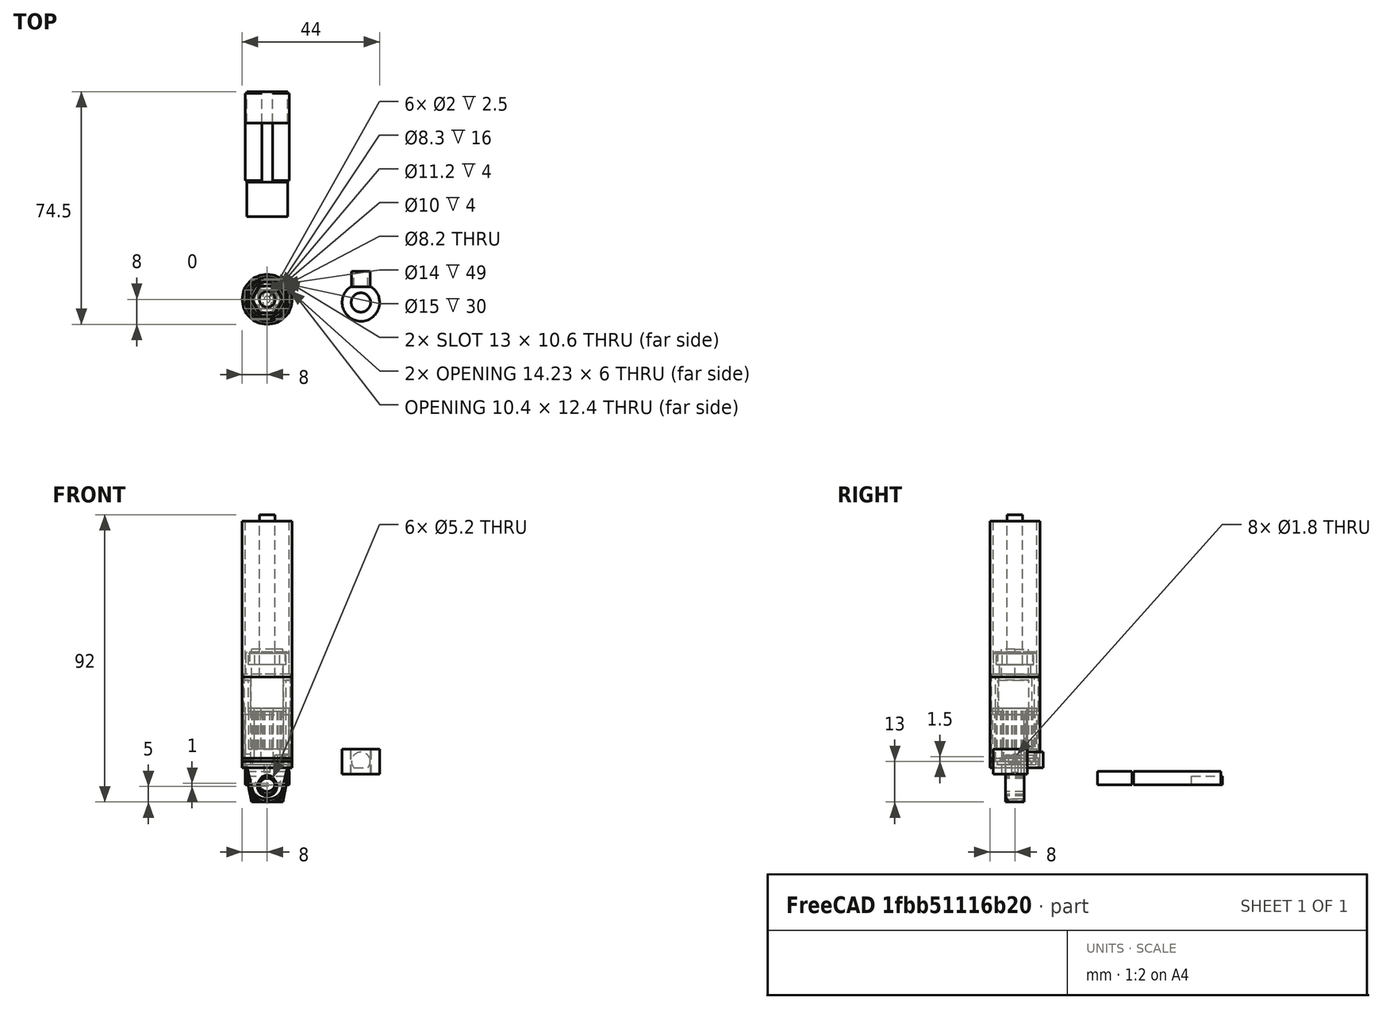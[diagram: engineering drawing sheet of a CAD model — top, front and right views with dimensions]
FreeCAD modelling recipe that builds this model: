
FCSTD DOCUMENT  (FreeCAD 0.18.4R)
Label: crane-cylinder
License: CC-BY 3.0
LicenseURL: http://creativecommons.org/licenses/by/3.0/
objects: Part::Cylinder×114, Part::Cut×95, Part::Box×52, Part::MultiFuse×50, Part::Fillet×11, Part::Cone×10, Part::Chamfer×9, Part::Extrusion×2, App::DocumentObjectGroup×1, Part::RegularPolygon×1, Part::Feature×1
note: 345 computed .brp shape members not serialized (recipe doc carries the construction recipe); baked Part::Feature solids carry a one-line shape summary decoded from their .brp

FEATURE [Part::Cylinder] Cylinder007
  Angle = 360
  AttacherType = Attacher::AttachEngine3D
  Height = 26
  Radius = 7.5
FEATURE [Part::Box] Box  label="Cube"
  AttacherType = Attacher::AttachEngine3D
  Height = 26
  Length = 10.4
  Placement = pos=(-5.2,-8.05,0) rot=(0,0,1;0rad)
  Width = 16.1
FEATURE [Part::Cut] Cut005
  Base = -> Cylinder007
  Refine = true
  Tool = -> Box
FEATURE [Part::Cone] Cone
  Angle = 360
  AttacherType = Attacher::AttachEngine3D
  Height = 13
  Placement = pos=(0,0,-13) rot=(0,0,1;0rad)
  Radius1 = 5
  Radius2 = 7.5
FEATURE [Part::Box] Box001  label="Cube001"
  AttacherType = Attacher::AttachEngine3D
  Height = 12
  Length = 16
  Placement = pos=(-8,3,-12) rot=(0,0,1;0rad)
  Width = 10
FEATURE [Part::Box] Box002  label="Cube002"
  AttacherType = Attacher::AttachEngine3D
  Height = 12
  Length = 16
  Placement = pos=(-8,-13,-12) rot=(0,0,1;0rad)
  Width = 10
FEATURE [Part::MultiFuse] Fusion001
  Placement = pos=(0,0,-1) rot=(0,0,1;0rad)
  Refine = true
  Shapes = -> [Box002,Box001]
FEATURE [Part::Cylinder] Cylinder008
  Angle = 360
  AttacherType = Attacher::AttachEngine3D
  Height = 10
  Placement = pos=(0,5,-8) rot=(1,0,0;1.5708rad)
  Radius = 3.1
FEATURE [Part::Cylinder] Cylinder009
  Angle = 360
  AttacherType = Attacher::AttachEngine3D
  Height = 2
  Placement = pos=(0,0,-2) rot=(0,0,1;0rad)
  Radius = 7.5
FEATURE [Part::Cut] Cut006
  Base = -> Cone
  Refine = true
  Tool = -> Fusion001
FEATURE [Part::MultiFuse] Fusion002
  Refine = true
  Shapes = -> [Cut005,Cut006,Cylinder009]
FEATURE [Part::Cut] Cut007
  Base = -> Fusion002
  Refine = true
  Tool = -> Cylinder008
FEATURE [Part::Box] Box003  label="Cube005"
  AttacherType = Attacher::AttachEngine3D
  Height = 28
  Length = 14
  Placement = pos=(-7,1.5,-2) rot=(0,0,1;0rad)
  Width = 6
FEATURE [Part::Cylinder] Cylinder010
  Angle = 360
  AttacherType = Attacher::AttachEngine3D
  Height = 28
  Placement = pos=(0,0,-2) rot=(0,0,1;0rad)
  Radius = 7.7
FEATURE [Part::Cylinder] Cylinder012
  Angle = 360
  AttacherType = Attacher::AttachEngine3D
  Height = 16
  Radius = 7.5
FEATURE [Part::Cylinder] Cylinder013
  Angle = 360
  AttacherType = Attacher::AttachEngine3D
  Height = 16
  Radius = 6.25
FEATURE [Part::Cut] Cut008
  Base = -> Cylinder012
  Refine = true
  Tool = -> Cylinder013
FEATURE [Part::MultiFuse] Fusion003
  Refine = true
  Shapes = -> [Cut007,Cut008]
FEATURE [Part::Box] Box004  label="Cube006"
  AttacherType = Attacher::AttachEngine3D
  Height = 2.5
  Length = 10
  Placement = pos=(2,-2,-0.5) rot=(0,0,1;0rad)
  Width = 4
FEATURE [Part::Cut] Cut009
  Base = -> Fusion003
  Placement = pos=(0,40,0) rot=(-1,0,0;1.5708rad)
  Refine = true
  Tool = -> Box004
FEATURE [Part::Cut] Cut010  label="cylinder-motor-holder-SUPPORT_"
  Base = -> Box003
  Placement = pos=(0,40,0) rot=(-1,0,0;1.5708rad)
  Refine = true
  Tool = -> Cylinder010
FEATURE [Part::Cylinder] Cylinder014
  Angle = 360
  AttacherType = Attacher::AttachEngine3D
  Height = 5
  Placement = pos=(0,0,4) rot=(0,0,1;0rad)
  Radius = 3
FEATURE [Part::Cylinder] Cylinder015
  Angle = 360
  AttacherType = Attacher::AttachEngine3D
  Height = 8
  Placement = pos=(0,4,0) rot=(1,0,0;1.5708rad)
  Radius = 6
FEATURE [Part::Cylinder] Cylinder016
  Angle = 360
  AttacherType = Attacher::AttachEngine3D
  Height = 8
  Placement = pos=(0,4,0) rot=(1,0,0;1.5708rad)
  Radius = 3.1
FEATURE [Part::Cut] Cut011
  Base = -> Cylinder015
  Placement = pos=(0,0,-1) rot=(0,0,1;0rad)
  Refine = true
  Tool = -> Cylinder016
FEATURE [Part::Box] Box005  label="Cube007"
  AttacherType = Attacher::AttachEngine3D
  Height = 10
  Length = 6
  Placement = pos=(-3,2,4) rot=(0,0,1;0rad)
  Width = 2
FEATURE [Part::Box] Box006  label="Cube009"
  AttacherType = Attacher::AttachEngine3D
  Height = 10
  Length = 10
  Placement = pos=(-5,-5,4) rot=(0,0,1;0rad)
  Width = 10
FEATURE [Part::Cut] Cut012
  Base = -> Cut011
  Refine = true
  Tool = -> Box006
FEATURE [Part::Cut] Cut013
  Base = -> Cylinder014
  Refine = true
  Tool = -> Box005
FEATURE [Part::MultiFuse] Fusion004  label="cylinder-piston-head-attach"
  Placement = pos=(30,0,0) rot=(-1,0,0;1.5708rad)
  Refine = true
  Shapes = -> [Cut012,Cut013]
FEATURE [Part::Fillet] Fillet002  label="cylinder-motor-holder_"
  Base = -> Cut009
  Edges = 3 edges r=3: [Edge56,Edge61,Edge65]
FEATURE [Part::Box] Box008  label="Cube010"
  AttacherType = Attacher::AttachEngine3D
  Height = 3
  Length = 16
  Placement = pos=(-8,56,-7.5) rot=(0,0,1;0rad)
  Width = 10
FEATURE [Part::Cut] Cut  label="cylinder-motor-holder-OLD"
  Base = -> Fillet002
  Placement = pos=(0,0,-40) rot=(1,0,0;1.5708rad)
  Refine = true
  Tool = -> Box008
FEATURE [Part::Box] Box009  label="Cube011"
  AttacherType = Attacher::AttachEngine3D
  Height = 4.3
  Length = 13
  Placement = pos=(-6.5,26.5,-7.5) rot=(0,0,1;0rad)
  Width = 11
FEATURE [Part::Box] Box010  label="Cube012"
  AttacherType = Attacher::AttachEngine3D
  Height = 2.8
  Length = 13
  Placement = pos=(-6.5,56.5,-7.5) rot=(0,0,1;0rad)
  Width = 10
FEATURE [Part::MultiFuse] Fusion  label="cylinder-motor-holder-SUPPORT"
  Refine = true
  Shapes = -> [Box009,Box010]
FEATURE [Part::Cylinder] Cylinder
  Angle = 360
  AttacherType = Attacher::AttachEngine3D
  Height = 4
  Radius = 7.05
FEATURE [Part::Cylinder] Cylinder001
  Angle = 360
  AttacherType = Attacher::AttachEngine3D
  Height = 4
  Radius = 4.1
FEATURE [Part::Cut] Cut014
  Base = -> Cylinder
  Refine = true
  Tool = -> Cylinder001
FEATURE [Part::Cylinder] Cylinder002
  Angle = 360
  AttacherType = Attacher::AttachEngine3D
  Height = 1
  Placement = pos=(0,0,6) rot=(0,0,1;0rad)
  Radius = 8
FEATURE [Part::Cylinder] Cylinder003
  Angle = 360
  AttacherType = Attacher::AttachEngine3D
  Height = 1
  Placement = pos=(0,0,6) rot=(0,0,1;0rad)
  Radius = 6
FEATURE [Part::Cut] Cut001
  Base = -> Cylinder002
  Placement = pos=(0,0,-6) rot=(0,0,1;0rad)
  Refine = true
  Tool = -> Cylinder003
FEATURE [Part::MultiFuse] Fusion005  label="Union"
  Refine = true
  Shapes = -> [Cut001,Cut014]
FEATURE [Part::Chamfer] Chamfer  label="cylinder-jacket-cap"
  Base = -> Fusion005
  Edges = 1 edges r=1: [Edge9]
FEATURE [Part::Cylinder] Cylinder019
  Angle = 360
  AttacherType = Attacher::AttachEngine3D
  Height = 27
  Radius = 8
FEATURE [Part::Box] Box011  label="Cube013"
  AttacherType = Attacher::AttachEngine3D
  Height = 27
  Length = 10.4
  Placement = pos=(-5.2,-6.2,0) rot=(0,0,1;0rad)
  Width = 12.4
FEATURE [Part::Cone] Cone001
  Angle = 360
  AttacherType = Attacher::AttachEngine3D
  Height = 13
  Placement = pos=(0,0,-13) rot=(0,0,1;0rad)
  Radius1 = 5
  Radius2 = 7.5
FEATURE [Part::Box] Box012  label="Cube014"
  AttacherType = Attacher::AttachEngine3D
  Height = 12
  Length = 16
  Placement = pos=(-8,3,-12) rot=(0,0,1;0rad)
  Width = 10
FEATURE [Part::Box] Box013  label="Cube015"
  AttacherType = Attacher::AttachEngine3D
  Height = 12
  Length = 16
  Placement = pos=(-8,-13,-12) rot=(0,0,1;0rad)
  Width = 10
FEATURE [Part::MultiFuse] Fusion006
  Placement = pos=(0,0,-1) rot=(0,0,1;0rad)
  Refine = true
  Shapes = -> [Box013,Box012]
FEATURE [Part::Cut] Cut016
  Base = -> Cone001
  Refine = true
  Tool = -> Fusion006
FEATURE [Part::Cylinder] Cylinder022
  Angle = 360
  AttacherType = Attacher::AttachEngine3D
  Height = 17
  Radius = 8
FEATURE [Part::Cylinder] Cylinder023
  Angle = 360
  AttacherType = Attacher::AttachEngine3D
  Height = 17
  Radius = 6.5
FEATURE [Part::Cut] Cut020
  Base = -> Cylinder022
  Refine = true
  Tool = -> Cylinder023
FEATURE [Part::Fillet] Fillet
  Base = -> Box011
  Edges = 4 edges r=1: [Edge1,Edge3,Edge5,Edge7]
FEATURE [Part::Cut] Cut021
  Base = -> Cylinder019
  Refine = true
  Tool = -> Fillet
FEATURE [Part::MultiFuse] Fusion009
  Refine = true
  Shapes = -> [Cut020,Cut021]
FEATURE [Part::Cylinder] Cylinder028
  Angle = 360
  AttacherType = Attacher::AttachEngine3D
  Height = 27
  Radius = 8
FEATURE [Part::Box] Box017  label="Cube019"
  AttacherType = Attacher::AttachEngine3D
  Height = 27
  Length = 10.4
  Placement = pos=(-5.2,-6.2,0) rot=(0,0,1;0rad)
  Width = 12.4
FEATURE [Part::Cylinder] Cylinder029
  Angle = 360
  AttacherType = Attacher::AttachEngine3D
  Height = 17
  Radius = 8
FEATURE [Part::Cylinder] Cylinder030
  Angle = 360
  AttacherType = Attacher::AttachEngine3D
  Height = 17
  Radius = 6.5
FEATURE [Part::Cut] Cut025
  Base = -> Cylinder029
  Refine = true
  Tool = -> Cylinder030
FEATURE [Part::Fillet] Fillet004
  Base = -> Box017
  Edges = 4 edges r=1: [Edge1,Edge3,Edge5,Edge7]
FEATURE [Part::Cut] Cut026
  Base = -> Cylinder028
  Refine = true
  Tool = -> Fillet004
FEATURE [Part::MultiFuse] Fusion010
  Refine = true
  Shapes = -> [Cut025,Cut026]
FEATURE [Part::Cylinder] Cylinder024
  Angle = 360
  AttacherType = Attacher::AttachEngine3D
  Height = 27
  Radius = 8
FEATURE [Part::Cut] Cut027  label="MOTOR"
  Base = -> Cylinder024
  Refine = true
  Tool = -> Fusion010
FEATURE [Part::Cylinder] Cylinder031
  Angle = 360
  AttacherType = Attacher::AttachEngine3D
  Height = 4
  Radius = 5.6
FEATURE [Part::Cylinder] Cylinder032
  Angle = 360
  AttacherType = Attacher::AttachEngine3D
  Height = 20
  Radius = 6.95
FEATURE [Part::Cylinder] Cylinder033
  Angle = 360
  AttacherType = Attacher::AttachEngine3D
  Height = 8
  Radius = 5
FEATURE [Part::MultiFuse] Fusion011
  Refine = true
  Shapes = -> [Cylinder031,Cylinder033]
FEATURE [Part::Cut] Cut028
  Base = -> Cylinder032
  Refine = true
  Tool = -> Fusion011
FEATURE [Part::Box] Box018  label="Cube020"
  AttacherType = Attacher::AttachEngine3D
  Height = 26
  Length = 10.4
  Placement = pos=(-5.2,-8.05,8) rot=(0,0,1;0rad)
  Width = 16.1
FEATURE [Part::Cylinder] Cylinder034
  Angle = 360
  AttacherType = Attacher::AttachEngine3D
  Height = 16
  Radius = 7.5
FEATURE [Part::Box] Box019  label="Cube021"
  AttacherType = Attacher::AttachEngine3D
  Height = 26
  Length = 10.6
  Placement = pos=(-5.3,-8.05,-1) rot=(0,0,1;0rad)
  Width = 16.1
FEATURE [Part::Cut] Cut030
  Base = -> Cylinder034
  Placement = pos=(0,0,-1) rot=(0,0,1;0rad)
  Refine = true
  Tool = -> Box019
FEATURE [Part::Cone] Cone002
  Angle = 360
  AttacherType = Attacher::AttachEngine3D
  Height = 13
  Placement = pos=(0,0,-13) rot=(0,0,1;0rad)
  Radius1 = 5
  Radius2 = 7.5
FEATURE [Part::Box] Box020  label="Cube022"
  AttacherType = Attacher::AttachEngine3D
  Height = 12
  Length = 16
  Placement = pos=(-8,3,-12) rot=(0,0,1;0rad)
  Width = 10
FEATURE [Part::Box] Box021  label="Cube023"
  AttacherType = Attacher::AttachEngine3D
  Height = 12
  Length = 16
  Placement = pos=(-8,-13,-12) rot=(0,0,1;0rad)
  Width = 10
FEATURE [Part::MultiFuse] Fusion012
  Placement = pos=(0,0,-1) rot=(0,0,1;0rad)
  Refine = true
  Shapes = -> [Box021,Box020]
FEATURE [Part::Cylinder] Cylinder035
  Angle = 360
  AttacherType = Attacher::AttachEngine3D
  Height = 10
  Placement = pos=(0,5,-8) rot=(1,0,0;1.5708rad)
  Radius = 2.6
FEATURE [Part::Cylinder] Cylinder036
  Angle = 360
  AttacherType = Attacher::AttachEngine3D
  Height = 2
  Placement = pos=(0,0,-2) rot=(0,0,1;0rad)
  Radius = 7.5
FEATURE [Part::Cut] Cut031
  Base = -> Cone002
  Refine = true
  Tool = -> Fusion012
FEATURE [Part::Cylinder] Cylinder037
  Angle = 360
  AttacherType = Attacher::AttachEngine3D
  Height = 15
  Radius = 7.5
FEATURE [Part::Cylinder] Cylinder038
  Angle = 360
  AttacherType = Attacher::AttachEngine3D
  Height = 19
  Radius = 6.5
FEATURE [Part::Cut] Cut033
  Base = -> Cylinder037
  Refine = true
  Tool = -> Cylinder038
FEATURE [Part::MultiFuse] Fusion013
  Refine = true
  Shapes = -> [Cut031,Cylinder036]
FEATURE [Part::Cut] Cut034
  Base = -> Fusion013
  Refine = true
  Tool = -> Cylinder035
FEATURE [Part::Cylinder] Cylinder039
  Angle = 360
  AttacherType = Attacher::AttachEngine3D
  Height = 1
  Placement = pos=(0,0,-1) rot=(0,0,1;0rad)
  Radius = 5.5
FEATURE [Part::Cut] Cut035
  Base = -> Cut034
  Refine = true
  Tool = -> Cylinder039
FEATURE [Part::Box] Box022  label="Cube024"
  AttacherType = Attacher::AttachEngine3D
  Height = 3
  Length = 10
  Placement = pos=(2,-3,-1) rot=(0,0,1;0rad)
  Width = 6
FEATURE [Part::Cylinder] Cylinder042
  Angle = 360
  AttacherType = Attacher::AttachEngine3D
  Height = 13
  Placement = pos=(0,0,7) rot=(0,0,1;0rad)
  Radius = 7.45
FEATURE [Part::MultiFuse] Fusion016
  Refine = true
  Shapes = -> [Cut028,Cylinder042]
FEATURE [Part::Fillet] Fillet005
  Base = -> Cut035
  Edges = 3 edges r=4: [Edge1,Edge3,Edge5]
FEATURE [Part::MultiFuse] Fusion017
  Refine = true
  Shapes = -> [Fillet005,Cut030,Cut033]
FEATURE [Part::Cut] Cut039
  Base = -> Fusion017
  Refine = true
  Tool = -> Box022
FEATURE [Part::Cut] Cut041
  Base = -> Fusion016
  Refine = true
  Tool = -> Box018
FEATURE [Part::Cylinder] Cylinder045
  Angle = 360
  AttacherType = Attacher::AttachEngine3D
  Height = 8
  Radius = 5
FEATURE [Part::Cut] Cut042
  Base = -> Cut041
  Placement = pos=(0,0,35) rot=(1,0,0;3.14159rad)
  Refine = true
  Tool = -> Cylinder045
FEATURE [Part::Chamfer] Chamfer001  label="cylinder-motor-holder-bearing-support"
  Base = -> Cut042
  Edges = 1 edges r=0.5: [Edge19]
FEATURE [Part::Cylinder] Cylinder046
  Angle = 360
  AttacherType = Attacher::AttachEngine3D
  Height = 16
  Radius = 7.5
FEATURE [Part::Box] Box023  label="Cube025"
  AttacherType = Attacher::AttachEngine3D
  Height = 26
  Length = 10.6
  Placement = pos=(-5.3,-8.05,-1) rot=(0,0,1;0rad)
  Width = 16.1
FEATURE [Part::Cut] Cut043
  Base = -> Cylinder046
  Placement = pos=(0,0,-1) rot=(0,0,1;0rad)
  Refine = true
  Tool = -> Box023
FEATURE [Part::Cone] Cone003
  Angle = 360
  AttacherType = Attacher::AttachEngine3D
  Height = 13
  Placement = pos=(0,0,-13) rot=(0,0,1;0rad)
  Radius1 = 5
  Radius2 = 7.5
FEATURE [Part::Box] Box024  label="Cube026"
  AttacherType = Attacher::AttachEngine3D
  Height = 12
  Length = 16
  Placement = pos=(-8,3,-12) rot=(0,0,1;0rad)
  Width = 10
FEATURE [Part::Box] Box025  label="Cube027"
  AttacherType = Attacher::AttachEngine3D
  Height = 12
  Length = 16
  Placement = pos=(-8,-13,-12) rot=(0,0,1;0rad)
  Width = 10
FEATURE [Part::MultiFuse] Fusion018
  Placement = pos=(0,0,-1) rot=(0,0,1;0rad)
  Refine = true
  Shapes = -> [Box025,Box024]
FEATURE [Part::Cylinder] Cylinder047
  Angle = 360
  AttacherType = Attacher::AttachEngine3D
  Height = 10
  Placement = pos=(0,5,-8) rot=(1,0,0;1.5708rad)
  Radius = 2.6
FEATURE [Part::Cylinder] Cylinder048
  Angle = 360
  AttacherType = Attacher::AttachEngine3D
  Height = 2
  Placement = pos=(0,0,-2) rot=(0,0,1;0rad)
  Radius = 7.5
FEATURE [Part::Cut] Cut044
  Base = -> Cone003
  Refine = true
  Tool = -> Fusion018
FEATURE [Part::Cylinder] Cylinder049
  Angle = 360
  AttacherType = Attacher::AttachEngine3D
  Height = 15
  Radius = 7.5
FEATURE [Part::Cylinder] Cylinder050
  Angle = 360
  AttacherType = Attacher::AttachEngine3D
  Height = 19
  Radius = 6.5
FEATURE [Part::Cut] Cut045
  Base = -> Cylinder049
  Refine = true
  Tool = -> Cylinder050
FEATURE [Part::MultiFuse] Fusion019
  Refine = true
  Shapes = -> [Cut044,Cylinder048]
FEATURE [Part::Cut] Cut046
  Base = -> Fusion019
  Refine = true
  Tool = -> Cylinder047
FEATURE [Part::Cylinder] Cylinder051
  Angle = 360
  AttacherType = Attacher::AttachEngine3D
  Height = 1
  Placement = pos=(0,0,-1) rot=(0,0,1;0rad)
  Radius = 5.5
FEATURE [Part::Cut] Cut047
  Base = -> Cut046
  Refine = true
  Tool = -> Cylinder051
FEATURE [Part::Box] Box026  label="Cube028"
  AttacherType = Attacher::AttachEngine3D
  Height = 3
  Length = 10
  Placement = pos=(3.46045,-1.01256,-1) rot=(0,0,1;0.698132rad)
  Width = 6
FEATURE [Part::Fillet] Fillet006
  Base = -> Cut047
  Edges = 3 edges r=4: [Edge1,Edge3,Edge5]
FEATURE [Part::MultiFuse] Fusion020
  Refine = true
  Shapes = -> [Fillet006,Cut043,Cut045]
FEATURE [Part::Cut] Cut048
  Base = -> Fusion020
  Refine = true
  Tool = -> Box026
FEATURE [Part::Cylinder] Cylinder052
  Angle = 360
  AttacherType = Attacher::AttachEngine3D
  Height = 16
  Radius = 7.5
FEATURE [Part::Box] Box027  label="Cube029"
  AttacherType = Attacher::AttachEngine3D
  Height = 26
  Length = 10.6
  Placement = pos=(-5.3,-8.05,-1) rot=(0,0,1;0rad)
  Width = 16.1
FEATURE [Part::Cut] Cut049
  Base = -> Cylinder052
  Placement = pos=(0,0,-1) rot=(0,0,1;0rad)
  Refine = true
  Tool = -> Box027
FEATURE [Part::Cone] Cone004
  Angle = 360
  AttacherType = Attacher::AttachEngine3D
  Height = 12
  Placement = pos=(0,0,-12) rot=(0,0,1;0rad)
  Radius1 = 5
  Radius2 = 7.5
FEATURE [Part::Box] Box028  label="Cube030"
  AttacherType = Attacher::AttachEngine3D
  Height = 12
  Length = 16
  Placement = pos=(-8,3,-12) rot=(0,0,1;0rad)
  Width = 10
FEATURE [Part::Box] Box029  label="Cube031"
  AttacherType = Attacher::AttachEngine3D
  Height = 12
  Length = 16
  Placement = pos=(-8,-13,-12) rot=(0,0,1;0rad)
  Width = 10
FEATURE [Part::MultiFuse] Fusion021
  Placement = pos=(0,0,-1) rot=(0,0,1;0rad)
  Refine = true
  Shapes = -> [Box029,Box028]
FEATURE [Part::Cylinder] Cylinder053
  Angle = 360
  AttacherType = Attacher::AttachEngine3D
  Height = 10
  Placement = pos=(0,5,-7) rot=(1,0,0;1.5708rad)
  Radius = 2.6
FEATURE [Part::Cylinder] Cylinder054
  Angle = 360
  AttacherType = Attacher::AttachEngine3D
  Height = 2
  Placement = pos=(0,0,-2) rot=(0,0,1;0rad)
  Radius = 7.5
FEATURE [Part::Cut] Cut050
  Base = -> Cone004
  Refine = true
  Tool = -> Fusion021
FEATURE [Part::Cylinder] Cylinder055
  Angle = 360
  AttacherType = Attacher::AttachEngine3D
  Height = 15
  Radius = 7.5
FEATURE [Part::Cylinder] Cylinder056
  Angle = 360
  AttacherType = Attacher::AttachEngine3D
  Height = 19
  Radius = 6.5
FEATURE [Part::Cut] Cut051
  Base = -> Cylinder055
  Refine = true
  Tool = -> Cylinder056
FEATURE [Part::MultiFuse] Fusion022
  Refine = true
  Shapes = -> [Cut050,Cylinder054]
FEATURE [Part::Cut] Cut052
  Base = -> Fusion022
  Refine = true
  Tool = -> Cylinder053
FEATURE [Part::Cylinder] Cylinder057
  Angle = 360
  AttacherType = Attacher::AttachEngine3D
  Height = 1
  Placement = pos=(0,0,-1) rot=(0,0,1;0rad)
  Radius = 5.5
FEATURE [Part::Cut] Cut053
  Base = -> Cut052
  Refine = true
  Tool = -> Cylinder057
FEATURE [Part::Box] Box030  label="Cube032"
  AttacherType = Attacher::AttachEngine3D
  Height = 3
  Length = 10
  Placement = pos=(2,-3,-1) rot=(0,0,1;0rad)
  Width = 6
FEATURE [Part::Fillet] Fillet007
  Base = -> Cut053
  Edges = 3 edges r=4: [Edge1,Edge3,Edge5]
FEATURE [Part::MultiFuse] Fusion023
  Refine = true
  Shapes = -> [Fillet007,Cut049,Cut051]
FEATURE [Part::Cut] Cut054
  Base = -> Fusion023
  Refine = true
  Tool = -> Box030
FEATURE [Part::Cylinder] Cylinder058
  Angle = 360
  AttacherType = Attacher::AttachEngine3D
  Height = 16
  Radius = 7.5
FEATURE [Part::Box] Box031  label="Cube033"
  AttacherType = Attacher::AttachEngine3D
  Height = 26
  Length = 10.6
  Placement = pos=(-5.3,-8.05,-1) rot=(0,0,1;0rad)
  Width = 16.1
FEATURE [Part::Cut] Cut055
  Base = -> Cylinder058
  Placement = pos=(0,0,-1) rot=(0,0,1;0rad)
  Refine = true
  Tool = -> Box031
FEATURE [Part::Cone] Cone005
  Angle = 360
  AttacherType = Attacher::AttachEngine3D
  Height = 12
  Placement = pos=(0,0,-12) rot=(0,0,1;0rad)
  Radius1 = 5
  Radius2 = 7.5
FEATURE [Part::Box] Box032  label="Cube034"
  AttacherType = Attacher::AttachEngine3D
  Height = 12
  Length = 16
  Placement = pos=(-8,3,-12) rot=(0,0,1;0rad)
  Width = 10
FEATURE [Part::Box] Box033  label="Cube035"
  AttacherType = Attacher::AttachEngine3D
  Height = 12
  Length = 16
  Placement = pos=(-8,-13,-12) rot=(0,0,1;0rad)
  Width = 10
FEATURE [Part::MultiFuse] Fusion024
  Placement = pos=(0,0,-1) rot=(0,0,1;0rad)
  Refine = true
  Shapes = -> [Box033,Box032]
FEATURE [Part::Cylinder] Cylinder059
  Angle = 360
  AttacherType = Attacher::AttachEngine3D
  Height = 10
  Placement = pos=(0,5,-7) rot=(1,0,0;1.5708rad)
  Radius = 2.6
FEATURE [Part::Cylinder] Cylinder060
  Angle = 360
  AttacherType = Attacher::AttachEngine3D
  Height = 2
  Placement = pos=(0,0,-2) rot=(0,0,1;0rad)
  Radius = 7.5
FEATURE [Part::Cut] Cut056
  Base = -> Cone005
  Refine = true
  Tool = -> Fusion024
FEATURE [Part::Cylinder] Cylinder061
  Angle = 360
  AttacherType = Attacher::AttachEngine3D
  Height = 15
  Radius = 7.5
FEATURE [Part::Cylinder] Cylinder062
  Angle = 360
  AttacherType = Attacher::AttachEngine3D
  Height = 19
  Radius = 6.5
FEATURE [Part::Cut] Cut057
  Base = -> Cylinder061
  Refine = true
  Tool = -> Cylinder062
FEATURE [Part::MultiFuse] Fusion025
  Refine = true
  Shapes = -> [Cut056,Cylinder060]
FEATURE [Part::Cut] Cut058
  Base = -> Fusion025
  Refine = true
  Tool = -> Cylinder059
FEATURE [Part::Cylinder] Cylinder063
  Angle = 360
  AttacherType = Attacher::AttachEngine3D
  Height = 1
  Placement = pos=(0,0,-1) rot=(0,0,1;0rad)
  Radius = 5.5
FEATURE [Part::Cut] Cut059
  Base = -> Cut058
  Refine = true
  Tool = -> Cylinder063
FEATURE [Part::Box] Box034  label="Cube036"
  AttacherType = Attacher::AttachEngine3D
  Height = 3
  Length = 10
  Placement = pos=(3.46045,-1.01256,-1) rot=(0,0,1;0.698132rad)
  Width = 6
FEATURE [Part::Fillet] Fillet008
  Base = -> Cut059
  Edges = 3 edges r=4: [Edge1,Edge3,Edge5]
FEATURE [Part::MultiFuse] Fusion026
  Refine = true
  Shapes = -> [Fillet008,Cut055,Cut057]
FEATURE [Part::Cut] Cut060  label="cylinder-main-motor-holder_"
  Base = -> Fusion026
  Refine = true
  Tool = -> Box034
FEATURE [Part::Cylinder] Cylinder064
  Angle = 360
  AttacherType = Attacher::AttachEngine3D
  Height = 4
  Radius = 7.05
FEATURE [Part::Cylinder] Cylinder065
  Angle = 360
  AttacherType = Attacher::AttachEngine3D
  Height = 4
  Radius = 4.15
FEATURE [Part::Cut] Cut061
  Base = -> Cylinder064
  Refine = true
  Tool = -> Cylinder065
FEATURE [Part::Cylinder] Cylinder066
  Angle = 360
  AttacherType = Attacher::AttachEngine3D
  Height = 1
  Placement = pos=(0,0,6) rot=(0,0,1;0rad)
  Radius = 8
FEATURE [Part::Cylinder] Cylinder067
  Angle = 360
  AttacherType = Attacher::AttachEngine3D
  Height = 1
  Placement = pos=(0,0,6) rot=(0,0,1;0rad)
  Radius = 6
FEATURE [Part::Cut] Cut062
  Base = -> Cylinder066
  Placement = pos=(0,0,-6) rot=(0,0,1;0rad)
  Refine = true
  Tool = -> Cylinder067
FEATURE [Part::MultiFuse] Fusion027  label="Union001"
  Refine = true
  Shapes = -> [Cut062,Cut061]
FEATURE [Part::Chamfer] Chamfer002  label="cylinder-jacket-cap001"
  Base = -> Fusion027
  Edges = 1 edges r=1: [Edge9]
FEATURE [Part::Cylinder] Cylinder068
  Angle = 45
  AttacherType = Attacher::AttachEngine3D
  Height = 16
  Radius = 7
FEATURE [Part::Cylinder] Cylinder069
  Angle = 360
  AttacherType = Attacher::AttachEngine3D
  Height = 16
  Radius = 4.15
FEATURE [Part::Cut] Cut063
  Base = -> Cylinder068
  Placement = pos=(0,0,1) rot=(0,0,1;0rad)
  Refine = true
  Tool = -> Cylinder069
FEATURE [Part::Cylinder] Cylinder070
  Angle = 360
  AttacherType = Attacher::AttachEngine3D
  Height = 16
  Radius = 7.05
FEATURE [Part::Cylinder] Cylinder071
  Angle = 360
  AttacherType = Attacher::AttachEngine3D
  Height = 16
  Radius = 6
FEATURE [Part::Cut] Cut064
  Base = -> Cylinder070
  Placement = pos=(0,0,1) rot=(0,0,1;0rad)
  Refine = true
  Tool = -> Cylinder071
FEATURE [Part::Chamfer] Chamfer003
  Base = -> Cut063
  Edges = 2 edges r=0.5: [Edge9,Edge12]
FEATURE [Part::Cylinder] Cylinder072
  Angle = 45
  AttacherType = Attacher::AttachEngine3D
  Height = 16
  Radius = 7
FEATURE [Part::Cylinder] Cylinder073
  Angle = 360
  AttacherType = Attacher::AttachEngine3D
  Height = 16
  Radius = 4.15
FEATURE [Part::Cut] Cut065
  Base = -> Cylinder072
  Placement = pos=(0,0,1) rot=(0,0,1;0rad)
  Refine = true
  Tool = -> Cylinder073
FEATURE [Part::Chamfer] Chamfer004
  Base = -> Cut065
  Edges = 2 edges r=0.5: [Edge9,Edge12]
  Placement = pos=(0,0,0) rot=(0,0,1;1.25664rad)
FEATURE [Part::Cylinder] Cylinder074
  Angle = 45
  AttacherType = Attacher::AttachEngine3D
  Height = 16
  Radius = 7
FEATURE [Part::Cylinder] Cylinder075
  Angle = 360
  AttacherType = Attacher::AttachEngine3D
  Height = 16
  Radius = 4.15
FEATURE [Part::Cut] Cut066
  Base = -> Cylinder074
  Placement = pos=(0,0,1) rot=(0,0,1;0rad)
  Refine = true
  Tool = -> Cylinder075
FEATURE [Part::Chamfer] Chamfer005
  Base = -> Cut066
  Edges = 2 edges r=0.5: [Edge9,Edge12]
  Placement = pos=(0,0,0) rot=(0,0,1;2.51327rad)
FEATURE [Part::Cylinder] Cylinder076
  Angle = 45
  AttacherType = Attacher::AttachEngine3D
  Height = 16
  Radius = 7
FEATURE [Part::Cylinder] Cylinder077
  Angle = 360
  AttacherType = Attacher::AttachEngine3D
  Height = 16
  Radius = 4.15
FEATURE [Part::Cut] Cut067
  Base = -> Cylinder076
  Placement = pos=(0,0,1) rot=(0,0,1;0rad)
  Refine = true
  Tool = -> Cylinder077
FEATURE [Part::Chamfer] Chamfer006
  Base = -> Cut067
  Edges = 2 edges r=0.5: [Edge9,Edge12]
  Placement = pos=(0,0,0) rot=(0,0,1;3.76991rad)
FEATURE [Part::Cylinder] Cylinder078
  Angle = 45
  AttacherType = Attacher::AttachEngine3D
  Height = 16
  Radius = 7
FEATURE [Part::Cylinder] Cylinder079
  Angle = 360
  AttacherType = Attacher::AttachEngine3D
  Height = 16
  Radius = 4.15
FEATURE [Part::Cut] Cut068
  Base = -> Cylinder078
  Placement = pos=(0,0,1) rot=(0,0,1;0rad)
  Refine = true
  Tool = -> Cylinder079
FEATURE [Part::Chamfer] Chamfer007
  Base = -> Cut068
  Edges = 2 edges r=0.5: [Edge9,Edge12]
  Placement = pos=(0,0,0) rot=(0,0,-1;1.25664rad)
FEATURE [Part::MultiFuse] Fusion028
  Refine = true
  Shapes = -> [Chamfer004,Chamfer003,Chamfer007,Chamfer005,Chamfer006]
FEATURE [Part::MultiFuse] Fusion029
  Refine = true
  Shapes = -> [Fusion028,Cut064]
FEATURE [Part::MultiFuse] Fusion030  label="cylinder-jacket-cap-001"
  Refine = true
  Shapes = -> [Chamfer002,Fusion029]
FEATURE [Part::Cylinder] Cylinder080
  Angle = 360
  AttacherType = Attacher::AttachEngine3D
  Height = 2
  Placement = pos=(0,0,-2) rot=(0,0,1;0rad)
  Radius = 7.5
FEATURE [Part::Cylinder] Cylinder081
  Angle = 360
  AttacherType = Attacher::AttachEngine3D
  Height = 16
  Radius = 7.5
FEATURE [Part::Box] Box035  label="Cube037"
  AttacherType = Attacher::AttachEngine3D
  Height = 26
  Length = 10.6
  Placement = pos=(-5.3,-8.05,-1) rot=(0,0,1;0rad)
  Width = 16.1
FEATURE [Part::Cut] Cut069
  Base = -> Cylinder081
  Placement = pos=(0,0,-1) rot=(0,0,1;0rad)
  Refine = true
  Tool = -> Box035
FEATURE [Part::Cone] Cone006
  Angle = 360
  AttacherType = Attacher::AttachEngine3D
  Height = 12
  Placement = pos=(0,0,-12) rot=(0,0,1;0rad)
  Radius1 = 5
  Radius2 = 7.5
FEATURE [Part::Box] Box036  label="Cube038"
  AttacherType = Attacher::AttachEngine3D
  Height = 12
  Length = 16
  Placement = pos=(-8,3,-12) rot=(0,0,1;0rad)
  Width = 10
FEATURE [Part::Box] Box037  label="Cube039"
  AttacherType = Attacher::AttachEngine3D
  Height = 12
  Length = 16
  Placement = pos=(-8,-13,-12) rot=(0,0,1;0rad)
  Width = 10
FEATURE [Part::MultiFuse] Fusion031
  Placement = pos=(0,0,-1) rot=(0,0,1;0rad)
  Refine = true
  Shapes = -> [Box037,Box036]
FEATURE [Part::Cylinder] Cylinder082
  Angle = 360
  AttacherType = Attacher::AttachEngine3D
  Height = 10
  Placement = pos=(0,5,-7) rot=(1,0,0;1.5708rad)
  Radius = 2.6
FEATURE [Part::Cut] Cut070
  Base = -> Cone006
  Refine = true
  Tool = -> Fusion031
FEATURE [Part::Cylinder] Cylinder083
  Angle = 360
  AttacherType = Attacher::AttachEngine3D
  Height = 15
  Radius = 7.5
FEATURE [Part::Cylinder] Cylinder084
  Angle = 360
  AttacherType = Attacher::AttachEngine3D
  Height = 19
  Radius = 6.5
FEATURE [Part::Cut] Cut071
  Base = -> Cylinder083
  Refine = true
  Tool = -> Cylinder084
FEATURE [Part::MultiFuse] Fusion032
  Refine = true
  Shapes = -> [Cut070,Cylinder080]
FEATURE [Part::Cut] Cut072
  Base = -> Fusion032
  Refine = true
  Tool = -> Cylinder082
FEATURE [Part::Cylinder] Cylinder085
  Angle = 360
  AttacherType = Attacher::AttachEngine3D
  Height = 1
  Placement = pos=(0,0,-1) rot=(0,0,1;0rad)
  Radius = 5.5
FEATURE [Part::Cut] Cut073
  Base = -> Cut072
  Refine = true
  Tool = -> Cylinder085
FEATURE [Part::Box] Box038  label="Cube040"
  AttacherType = Attacher::AttachEngine3D
  Height = 3
  Length = 10
  Placement = pos=(3.46045,-1.01256,-1) rot=(0,0,1;0.698132rad)
  Width = 6
FEATURE [Part::Fillet] Fillet009
  Base = -> Cut073
  Edges = 3 edges r=4: [Edge1,Edge3,Edge5]
FEATURE [Part::MultiFuse] Fusion033
  Refine = true
  Shapes = -> [Fillet009,Cut069,Cut071]
FEATURE [Part::Cut] Cut074  label="cylinder-motor-holder-short-30-deg-exit001"
  Base = -> Fusion033
  Refine = true
  Tool = -> Box038
FEATURE [Part::Box] Box039  label="Cube041"
  AttacherType = Attacher::AttachEngine3D
  Height = 27
  Length = 16
  Placement = pos=(-8,3,-12) rot=(0,0,1;0rad)
  Width = 10
FEATURE [Part::Box] Box040  label="Cube042"
  AttacherType = Attacher::AttachEngine3D
  Height = 27
  Length = 16
  Placement = pos=(-8,-9,-12) rot=(0,0,1;0rad)
  Width = 12
FEATURE [Part::Cylinder] Cylinder086
  Angle = 360
  AttacherType = Attacher::AttachEngine3D
  Height = 16
  Radius = 7.5
FEATURE [Part::Cylinder] Cylinder087
  Angle = 360
  AttacherType = Attacher::AttachEngine3D
  Height = 10
  Placement = pos=(0,5,-7) rot=(1,0,0;1.5708rad)
  Radius = 2.6
FEATURE [Part::Box] Box041  label="Cube043"
  AttacherType = Attacher::AttachEngine3D
  Height = 12
  Length = 16
  Placement = pos=(-8,-13,-12) rot=(0,0,1;0rad)
  Width = 10
FEATURE [Part::Box] Box042  label="Cube044"
  AttacherType = Attacher::AttachEngine3D
  Height = 12
  Length = 16
  Placement = pos=(-8,3,-12) rot=(0,0,1;0rad)
  Width = 10
FEATURE [Part::MultiFuse] Fusion034
  Placement = pos=(0,0,-1) rot=(0,0,1;0rad)
  Refine = true
  Shapes = -> [Box041,Box042]
FEATURE [Part::Box] Box043  label="Cube045"
  AttacherType = Attacher::AttachEngine3D
  Height = 26
  Length = 10.6
  Placement = pos=(-5.3,-8.05,-1) rot=(0,0,1;0rad)
  Width = 16.1
FEATURE [Part::Cylinder] Cylinder088
  Angle = 360
  AttacherType = Attacher::AttachEngine3D
  Height = 2
  Placement = pos=(0,0,-2) rot=(0,0,1;0rad)
  Radius = 7.5
FEATURE [Part::Cone] Cone007
  Angle = 360
  AttacherType = Attacher::AttachEngine3D
  Height = 12
  Placement = pos=(0,0,-12) rot=(0,0,1;0rad)
  Radius1 = 5
  Radius2 = 7.5
FEATURE [Part::Cut] Cut079
  Base = -> Cone007
  Refine = true
  Tool = -> Fusion034
FEATURE [Part::MultiFuse] Fusion036
  Refine = true
  Shapes = -> [Cut079,Cylinder088]
FEATURE [Part::Cut] Cut077
  Base = -> Fusion036
  Refine = true
  Tool = -> Cylinder087
FEATURE [Part::Cut] Cut080
  Base = -> Cylinder086
  Placement = pos=(0,0,-1) rot=(0,0,1;0rad)
  Refine = true
  Tool = -> Box043
FEATURE [Part::Cylinder] Cylinder089
  Angle = 360
  AttacherType = Attacher::AttachEngine3D
  Height = 19
  Radius = 6.5
FEATURE [Part::Cylinder] Cylinder090
  Angle = 360
  AttacherType = Attacher::AttachEngine3D
  Height = 15
  Radius = 7.5
FEATURE [Part::Cut] Cut078
  Base = -> Cylinder090
  Refine = true
  Tool = -> Cylinder089
FEATURE [Part::Cylinder] Cylinder091
  Angle = 360
  AttacherType = Attacher::AttachEngine3D
  Height = 1
  Placement = pos=(0,0,-1) rot=(0,0,1;0rad)
  Radius = 5.5
FEATURE [Part::Cut] Cut076
  Base = -> Cut077
  Refine = true
  Tool = -> Cylinder091
FEATURE [Part::Fillet] Fillet010
  Base = -> Cut076
  Edges = 3 edges r=4: [Edge1,Edge3,Edge5]
FEATURE [Part::MultiFuse] Fusion035
  Refine = true
  Shapes = -> [Fillet010,Cut080,Cut078]
FEATURE [Part::Box] Box044  label="Cube046"
  AttacherType = Attacher::AttachEngine3D
  Height = 3
  Length = 10
  Placement = pos=(3.46045,-1.01256,-1) rot=(0,0,1;0.698132rad)
  Width = 6
FEATURE [Part::Cut] Cut075  label="cylinder-motor-holder-short-30-deg-exit002"
  Base = -> Fusion035
  Refine = true
  Tool = -> Box044
FEATURE [Part::Cut] Cut081
  Base = -> Cut074
  Refine = true
  Tool = -> Box039
FEATURE [Part::Cut] Cut082  label="cylinder-main-motor-holder_B"
  Base = -> Cut075
  Refine = true
  Tool = -> Box040
FEATURE [Part::Cylinder] Cylinder092
  Angle = 360
  AttacherType = Attacher::AttachEngine3D
  Height = 10
  Placement = pos=(0,0,-3.5) rot=(0,0,1;0rad)
  Radius = 1
FEATURE [Part::Cut] Cut083
  Base = -> Cut081
  Refine = true
  Tool = -> Cylinder092
FEATURE [Part::Cylinder] Cylinder093
  Angle = 360
  AttacherType = Attacher::AttachEngine3D
  Height = 13
  Placement = pos=(-9,0,1.5) rot=(0,1,0;1.5708rad)
  Radius = 0.9
FEATURE [Part::Cut] Cut084  label="cylinder-main-motor-holder_A"
  Base = -> Cut083
  Refine = true
  Tool = -> Cylinder093
FEATURE [Part::Cylinder] Cylinder094
  Angle = 360
  AttacherType = Attacher::AttachEngine3D
  Height = 10
  Placement = pos=(0,0,-3.5) rot=(0,0,1;0rad)
  Radius = 1
FEATURE [Part::Cylinder] Cylinder095
  Angle = 360
  AttacherType = Attacher::AttachEngine3D
  Height = 18
  Placement = pos=(-9,0,1.5) rot=(0,1,0;1.5708rad)
  Radius = 0.9
FEATURE [Part::MultiFuse] Fusion037
  Refine = true
  Shapes = -> [Cylinder094,Cylinder095]
FEATURE [Part::Cut] Cut085  label="cylinder-main-motor-holder"
  Base = -> Cut060
  Refine = true
  Tool = -> Fusion037
FEATURE [Part::Cylinder] Cylinder096
  Angle = 360
  AttacherType = Attacher::AttachEngine3D
  Height = 10
  Placement = pos=(0,0,-3.5) rot=(0,0,1;0rad)
  Radius = 1
FEATURE [Part::Cylinder] Cylinder097
  Angle = 360
  AttacherType = Attacher::AttachEngine3D
  Height = 14
  Placement = pos=(-9,0,1.5) rot=(0,1,0;1.5708rad)
  Radius = 0.9
FEATURE [Part::MultiFuse] Fusion038
  Refine = true
  Shapes = -> [Cylinder096,Cylinder097]
FEATURE [Part::Cut] Cut086  label="cylinder-main-motor-holder-straight-exit"
  Base = -> Cut054
  Refine = true
  Tool = -> Fusion038
FEATURE [Part::Cylinder] Cylinder098
  Angle = 360
  AttacherType = Attacher::AttachEngine3D
  Height = 10
  Placement = pos=(0,0,-3.5) rot=(0,0,1;0rad)
  Radius = 1
FEATURE [Part::Cylinder] Cylinder099
  Angle = 360
  AttacherType = Attacher::AttachEngine3D
  Height = 18
  Placement = pos=(-9,0,1.5) rot=(0,1,0;1.5708rad)
  Radius = 0.9
FEATURE [Part::MultiFuse] Fusion039
  Refine = true
  Shapes = -> [Cylinder098,Cylinder099]
FEATURE [Part::Cut] Cut087  label="cylinder-main-motor-holder-long"
  Base = -> Cut048
  Refine = true
  Tool = -> Fusion039
FEATURE [App::DocumentObjectGroup] Group  label="backup"
  Group = -> [Fusion030,Cut086,Cut087,Cut010,Fusion004,Cut,Fusion,Cut016,Fusion009]
FEATURE [Part::Cylinder] Cylinder100
  Angle = 360
  AttacherType = Attacher::AttachEngine3D
  Height = 10
  Placement = pos=(0,0,-3.5) rot=(0,0,1;0rad)
  Radius = 1
FEATURE [Part::Cylinder] Cylinder101
  Angle = 360
  AttacherType = Attacher::AttachEngine3D
  Height = 14
  Placement = pos=(-9,0,0) rot=(0,1,0;1.5708rad)
  Radius = 0.9
FEATURE [Part::MultiFuse] Fusion040
  Refine = true
  Shapes = -> [Cylinder100,Cylinder101]
FEATURE [Part::Cut] Cut088  label="cylinder-extender-motor-holder"
  Base = -> Cut039
  Refine = true
  Tool = -> Fusion040
FEATURE [Part::Box] Box045  label="Cube047"
  AttacherType = Attacher::AttachEngine3D
  Height = 30
  Length = 16
  Placement = pos=(-8,-9,-14) rot=(0,0,1;0rad)
  Width = 12
FEATURE [Part::Box] Box046  label="Cube048"
  AttacherType = Attacher::AttachEngine3D
  Height = 30
  Length = 16
  Placement = pos=(-8,3,-14) rot=(0,0,1;0rad)
  Width = 10
FEATURE [Part::Cylinder] Cylinder102
  Angle = 360
  AttacherType = Attacher::AttachEngine3D
  Height = 16
  Radius = 7.5
FEATURE [Part::Box] Box047  label="Cube049"
  AttacherType = Attacher::AttachEngine3D
  Height = 26
  Length = 10.6
  Placement = pos=(-5.3,-8.05,-1) rot=(0,0,1;0rad)
  Width = 16.1
FEATURE [Part::Cut] Cut089
  Base = -> Cylinder102
  Placement = pos=(0,0,-1) rot=(0,0,1;0rad)
  Refine = true
  Tool = -> Box047
FEATURE [Part::Cone] Cone008
  Angle = 360
  AttacherType = Attacher::AttachEngine3D
  Height = 13
  Placement = pos=(0,0,-13) rot=(0,0,1;0rad)
  Radius1 = 5
  Radius2 = 7.5
FEATURE [Part::Box] Box048  label="Cube050"
  AttacherType = Attacher::AttachEngine3D
  Height = 12
  Length = 16
  Placement = pos=(-8,3,-12) rot=(0,0,1;0rad)
  Width = 10
FEATURE [Part::Box] Box049  label="Cube051"
  AttacherType = Attacher::AttachEngine3D
  Height = 12
  Length = 16
  Placement = pos=(-8,-13,-12) rot=(0,0,1;0rad)
  Width = 10
FEATURE [Part::MultiFuse] Fusion041
  Placement = pos=(0,0,-1) rot=(0,0,1;0rad)
  Refine = true
  Shapes = -> [Box049,Box048]
FEATURE [Part::Cylinder] Cylinder103
  Angle = 360
  AttacherType = Attacher::AttachEngine3D
  Height = 10
  Placement = pos=(0,5,-8) rot=(1,0,0;1.5708rad)
  Radius = 2.6
FEATURE [Part::Cylinder] Cylinder104
  Angle = 360
  AttacherType = Attacher::AttachEngine3D
  Height = 2
  Placement = pos=(0,0,-2) rot=(0,0,1;0rad)
  Radius = 7.5
FEATURE [Part::Cut] Cut090
  Base = -> Cone008
  Refine = true
  Tool = -> Fusion041
FEATURE [Part::Cylinder] Cylinder105
  Angle = 360
  AttacherType = Attacher::AttachEngine3D
  Height = 15
  Radius = 7.5
FEATURE [Part::Cylinder] Cylinder106
  Angle = 360
  AttacherType = Attacher::AttachEngine3D
  Height = 19
  Radius = 6.5
FEATURE [Part::Cut] Cut091
  Base = -> Cylinder105
  Refine = true
  Tool = -> Cylinder106
FEATURE [Part::MultiFuse] Fusion042
  Refine = true
  Shapes = -> [Cut090,Cylinder104]
FEATURE [Part::Cut] Cut092
  Base = -> Fusion042
  Refine = true
  Tool = -> Cylinder103
FEATURE [Part::Cylinder] Cylinder107
  Angle = 360
  AttacherType = Attacher::AttachEngine3D
  Height = 1
  Placement = pos=(0,0,-1) rot=(0,0,1;0rad)
  Radius = 5.5
FEATURE [Part::Cut] Cut093
  Base = -> Cut092
  Refine = true
  Tool = -> Cylinder107
FEATURE [Part::Fillet] Fillet011
  Base = -> Cut093
  Edges = 3 edges r=4: [Edge1,Edge3,Edge5]
FEATURE [Part::Box] Box050  label="Cube052"
  AttacherType = Attacher::AttachEngine3D
  Height = 3
  Length = 10
  Placement = pos=(2,-3,-1) rot=(0,0,1;0rad)
  Width = 6
FEATURE [Part::MultiFuse] Fusion043
  Refine = true
  Shapes = -> [Fillet011,Cut089,Cut091]
FEATURE [Part::Cut] Cut094
  Base = -> Fusion043
  Refine = true
  Tool = -> Box050
FEATURE [Part::Cylinder] Cylinder108
  Angle = 360
  AttacherType = Attacher::AttachEngine3D
  Height = 10
  Placement = pos=(0,0,-3.5) rot=(0,0,1;0rad)
  Radius = 1
FEATURE [Part::Cylinder] Cylinder109
  Angle = 360
  AttacherType = Attacher::AttachEngine3D
  Height = 14
  Placement = pos=(-9,0,0) rot=(0,1,0;1.5708rad)
  Radius = 0.9
FEATURE [Part::MultiFuse] Fusion044
  Refine = true
  Shapes = -> [Cylinder108,Cylinder109]
FEATURE [Part::Cut] Cut095  label="cylinder-extender-motor-holder001"
  Base = -> Cut094
  Refine = true
  Tool = -> Fusion044
FEATURE [Part::Cylinder] Cylinder110
  Angle = 360
  AttacherType = Attacher::AttachEngine3D
  Height = 16
  Radius = 7.5
FEATURE [Part::Box] Box051  label="Cube053"
  AttacherType = Attacher::AttachEngine3D
  Height = 26
  Length = 10.6
  Placement = pos=(-5.3,-8.05,-1) rot=(0,0,1;0rad)
  Width = 16.1
FEATURE [Part::Cut] Cut096
  Base = -> Cylinder110
  Placement = pos=(0,0,-1) rot=(0,0,1;0rad)
  Refine = true
  Tool = -> Box051
FEATURE [Part::Cone] Cone009
  Angle = 360
  AttacherType = Attacher::AttachEngine3D
  Height = 13
  Placement = pos=(0,0,-13) rot=(0,0,1;0rad)
  Radius1 = 5
  Radius2 = 7.5
FEATURE [Part::Box] Box052  label="Cube054"
  AttacherType = Attacher::AttachEngine3D
  Height = 12
  Length = 16
  Placement = pos=(-8,3,-12) rot=(0,0,1;0rad)
  Width = 10
FEATURE [Part::Box] Box053  label="Cube055"
  AttacherType = Attacher::AttachEngine3D
  Height = 12
  Length = 16
  Placement = pos=(-8,-13,-12) rot=(0,0,1;0rad)
  Width = 10
FEATURE [Part::MultiFuse] Fusion045
  Placement = pos=(0,0,-1) rot=(0,0,1;0rad)
  Refine = true
  Shapes = -> [Box053,Box052]
FEATURE [Part::Cylinder] Cylinder111
  Angle = 360
  AttacherType = Attacher::AttachEngine3D
  Height = 10
  Placement = pos=(0,5,-8) rot=(1,0,0;1.5708rad)
  Radius = 2.6
FEATURE [Part::Cylinder] Cylinder112
  Angle = 360
  AttacherType = Attacher::AttachEngine3D
  Height = 2
  Placement = pos=(0,0,-2) rot=(0,0,1;0rad)
  Radius = 7.5
FEATURE [Part::Cut] Cut097
  Base = -> Cone009
  Refine = true
  Tool = -> Fusion045
FEATURE [Part::Cylinder] Cylinder113
  Angle = 360
  AttacherType = Attacher::AttachEngine3D
  Height = 15
  Radius = 7.5
FEATURE [Part::Cylinder] Cylinder114
  Angle = 360
  AttacherType = Attacher::AttachEngine3D
  Height = 19
  Radius = 6.5
FEATURE [Part::Cut] Cut098
  Base = -> Cylinder113
  Refine = true
  Tool = -> Cylinder114
FEATURE [Part::MultiFuse] Fusion046
  Refine = true
  Shapes = -> [Cut097,Cylinder112]
FEATURE [Part::Cut] Cut099
  Base = -> Fusion046
  Refine = true
  Tool = -> Cylinder111
FEATURE [Part::Cylinder] Cylinder115
  Angle = 360
  AttacherType = Attacher::AttachEngine3D
  Height = 1
  Placement = pos=(0,0,-1) rot=(0,0,1;0rad)
  Radius = 5.5
FEATURE [Part::Cut] Cut100
  Base = -> Cut099
  Refine = true
  Tool = -> Cylinder115
FEATURE [Part::Fillet] Fillet012
  Base = -> Cut100
  Edges = 3 edges r=4: [Edge1,Edge3,Edge5]
FEATURE [Part::Box] Box054  label="Cube056"
  AttacherType = Attacher::AttachEngine3D
  Height = 3
  Length = 10
  Placement = pos=(2,-3,-1) rot=(0,0,1;0rad)
  Width = 6
FEATURE [Part::MultiFuse] Fusion047
  Refine = true
  Shapes = -> [Fillet012,Cut096,Cut098]
FEATURE [Part::Cut] Cut101
  Base = -> Fusion047
  Refine = true
  Tool = -> Box054
FEATURE [Part::Cylinder] Cylinder116
  Angle = 360
  AttacherType = Attacher::AttachEngine3D
  Height = 10
  Placement = pos=(0,0,-3.5) rot=(0,0,1;0rad)
  Radius = 1
FEATURE [Part::Cylinder] Cylinder117
  Angle = 360
  AttacherType = Attacher::AttachEngine3D
  Height = 14
  Placement = pos=(-9,0,0) rot=(0,1,0;1.5708rad)
  Radius = 0.9
FEATURE [Part::MultiFuse] Fusion048
  Refine = true
  Shapes = -> [Cylinder116,Cylinder117]
FEATURE [Part::Cut] Cut102  label="cylinder-extender-motor-holder002"
  Base = -> Cut101
  Refine = true
  Tool = -> Fusion048
FEATURE [Part::Cut] Cut103  label="cylinder-extender-motor-holder_B"
  Base = -> Cut095
  Refine = true
  Tool = -> Box045
FEATURE [Part::Cut] Cut104  label="cylinder-extender-motor-holder_A"
  Base = -> Cut102
  Refine = true
  Tool = -> Box046
FEATURE [Part::Cylinder] Cylinder118
  Angle = 360
  AttacherType = Attacher::AttachEngine3D
  Height = 4
  Radius = 5.7
FEATURE [Part::Cylinder] Cylinder119
  Angle = 360
  AttacherType = Attacher::AttachEngine3D
  Height = 20
  Radius = 6.85
FEATURE [Part::Cylinder] Cylinder120
  Angle = 360
  AttacherType = Attacher::AttachEngine3D
  Height = 8
  Radius = 5
FEATURE [Part::MultiFuse] Fusion049
  Refine = true
  Shapes = -> [Cylinder118,Cylinder120]
FEATURE [Part::Cut] Cut105
  Base = -> Cylinder119
  Refine = true
  Tool = -> Fusion049
FEATURE [Part::Box] Box055  label="Cube057"
  AttacherType = Attacher::AttachEngine3D
  Height = 26
  Length = 10.4
  Placement = pos=(-5.2,-8.05,8) rot=(0,0,1;0rad)
  Width = 16.1
FEATURE [Part::Cylinder] Cylinder121
  Angle = 360
  AttacherType = Attacher::AttachEngine3D
  Height = 13
  Placement = pos=(0,0,7) rot=(0,0,1;0rad)
  Radius = 7.45
FEATURE [Part::MultiFuse] Fusion050
  Refine = true
  Shapes = -> [Cut105,Cylinder121]
FEATURE [Part::Cut] Cut106
  Base = -> Fusion050
  Refine = true
  Tool = -> Box055
FEATURE [Part::Cylinder] Cylinder122
  Angle = 360
  AttacherType = Attacher::AttachEngine3D
  Height = 8
  Radius = 5
FEATURE [Part::Cut] Cut107
  Base = -> Cut106
  Placement = pos=(0,0,35) rot=(1,0,0;3.14159rad)
  Refine = true
  Tool = -> Cylinder122
FEATURE [Part::Chamfer] Chamfer008  label="cylinder-motor-holder-bearing-support-001"
  Base = -> Cut107
  Edges = 1 edges r=0.5: [Edge19]
FEATURE [Part::Cylinder] Cylinder123
  Angle = 360
  AttacherType = Attacher::AttachEngine3D
  Height = 79
  Radius = 2.5
FEATURE [Part::MultiFuse] Fusion051  label="motor_"
  Refine = true
  Shapes = -> [Cut027,Cylinder123]
FEATURE [Part::Cylinder] Cylinder124
  Angle = 360
  AttacherType = Attacher::AttachEngine3D
  Height = 3.5
  Placement = pos=(0,0,31) rot=(0,0,1;0rad)
  Radius = 6
FEATURE [Part::Cylinder] Cylinder125
  Angle = 360
  AttacherType = Attacher::AttachEngine3D
  Height = 3.5
  Placement = pos=(0,0,31) rot=(0,0,1;0rad)
  Radius = 4
FEATURE [Part::Cut] Cut108  label="bearing"
  Base = -> Cylinder124
  Refine = true
  Tool = -> Cylinder125
FEATURE [Part::RegularPolygon] RegularPolygon  label="Regular polygon"
  AttacherType = Attacher::AttachEngine3D
  Circumradius = 5
  Placement = pos=(0,0,27) rot=(0,0,1;0rad)
  Polygon = 6
FEATURE [Part::Extrusion] Extrude
  Base = -> RegularPolygon
  Dir = (0,0,1)
  DirMode = 2
  FaceMakerClass = Part::FaceMakerBullseye
  LengthFwd = 4
  LengthRev = 0
  Solid = true
  Symmetric = false
FEATURE [Part::Extrusion] Extrude001
  Base = -> RegularPolygon
  Dir = (0,0,1)
  DirMode = 2
  FaceMakerClass = Part::FaceMakerBullseye
  LengthFwd = 5
  LengthRev = 0
  Placement = pos=(0,0,4) rot=(0,0,1;0rad)
  Solid = true
  Symmetric = false
FEATURE [Part::Feature] Cut108001  label="bearing001"
  shape: bbox 12 x 12 x 3.5 mm, 4 faces (baked)
FEATURE [Part::Cut] Cut108002  label="retain_nut"
  Base = -> Extrude001
  Refine = true
  Tool = -> Cut108001
FEATURE [Part::MultiFuse] Fusion052  label="motor"
  Refine = true
  Shapes = -> [Extrude,Fusion051]
FEATURE [Part::Cylinder] Cylinder126
  Angle = 360
  AttacherType = Attacher::AttachEngine3D
  Height = 79
  Placement = pos=(0,0,-2) rot=(0,0,1;0rad)
  Radius = 8
FEATURE [Part::Cylinder] Cylinder127
  Angle = 360
  AttacherType = Attacher::AttachEngine3D
  Height = 30
  Placement = pos=(0,0,-2) rot=(0,0,1;0rad)
  Radius = 7.5
FEATURE [Part::Cylinder] Cylinder128
  Angle = 360
  AttacherType = Attacher::AttachEngine3D
  Height = 49
  Placement = pos=(0,0,28) rot=(0,0,1;0rad)
  Radius = 7
FEATURE [Part::MultiFuse] Fusion053
  Refine = true
  Shapes = -> [Cylinder128,Cylinder127]
FEATURE [Part::Cut] Cut108003  label="cylinder-jacket"
  Base = -> Cylinder126
  Refine = true
  Tool = -> Fusion053
